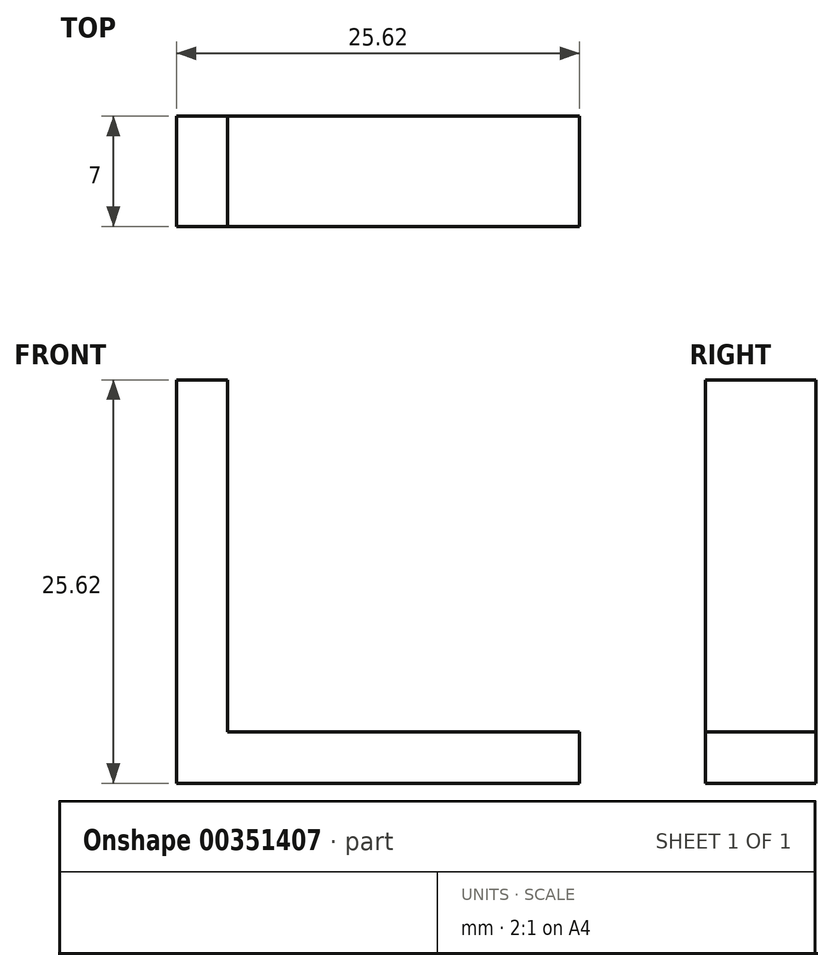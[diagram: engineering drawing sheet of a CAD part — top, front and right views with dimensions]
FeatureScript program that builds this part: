
annotation { "Feature Type Name" : "Feature", "Feature Type Description" : "" }
export const myFeature = defineFeature(function(context is Context, id is Id, definition is map)
    precondition{}
    {
        {
            var Q0;
            Q0=qCreatedBy(makeId("Front.planeOp"),FACE);
            var sketch = newSketch(context, id + "F0", { "sketchPlane" : qUnion([Q0])});
            skLineSegment(sketch, "E0.bottom", {"start": v(0, 0) * mm, "end": v(-3.26, 0) * mm});
            skLineSegment(sketch, "E0.top", {"start": v(0, 25.62) * mm, "end": v(-3.26, 25.62) * mm});
            skLineSegment(sketch, "E0.left", {"start": v(0, 0) * mm, "end": v(0, 25.62) * mm});
            skLineSegment(sketch, "E0.right", {"start": v(-3.26, 0) * mm, "end": v(-3.26, 25.62) * mm});
            skLineSegment(sketch, "E1.bottom", {"start": v(0, 0) * mm, "end": v(22.36, 0) * mm});
            skLineSegment(sketch, "E1.top", {"start": v(0, 3.26) * mm, "end": v(22.36, 3.26) * mm});
            skLineSegment(sketch, "E1.left", {"start": v(0, 0) * mm, "end": v(0, 3.26) * mm});
            skLineSegment(sketch, "E1.right", {"start": v(22.36, 0) * mm, "end": v(22.36, 3.26) * mm});
            skSolve(sketch);
        }
        {
            var Q0;
            Q0=qSketchRegion(id+"F0",true);
            extrude(context, id + "F1", {"entities" : qUnion([Q0]), "depth" : 7 * mm});
        }
    });
